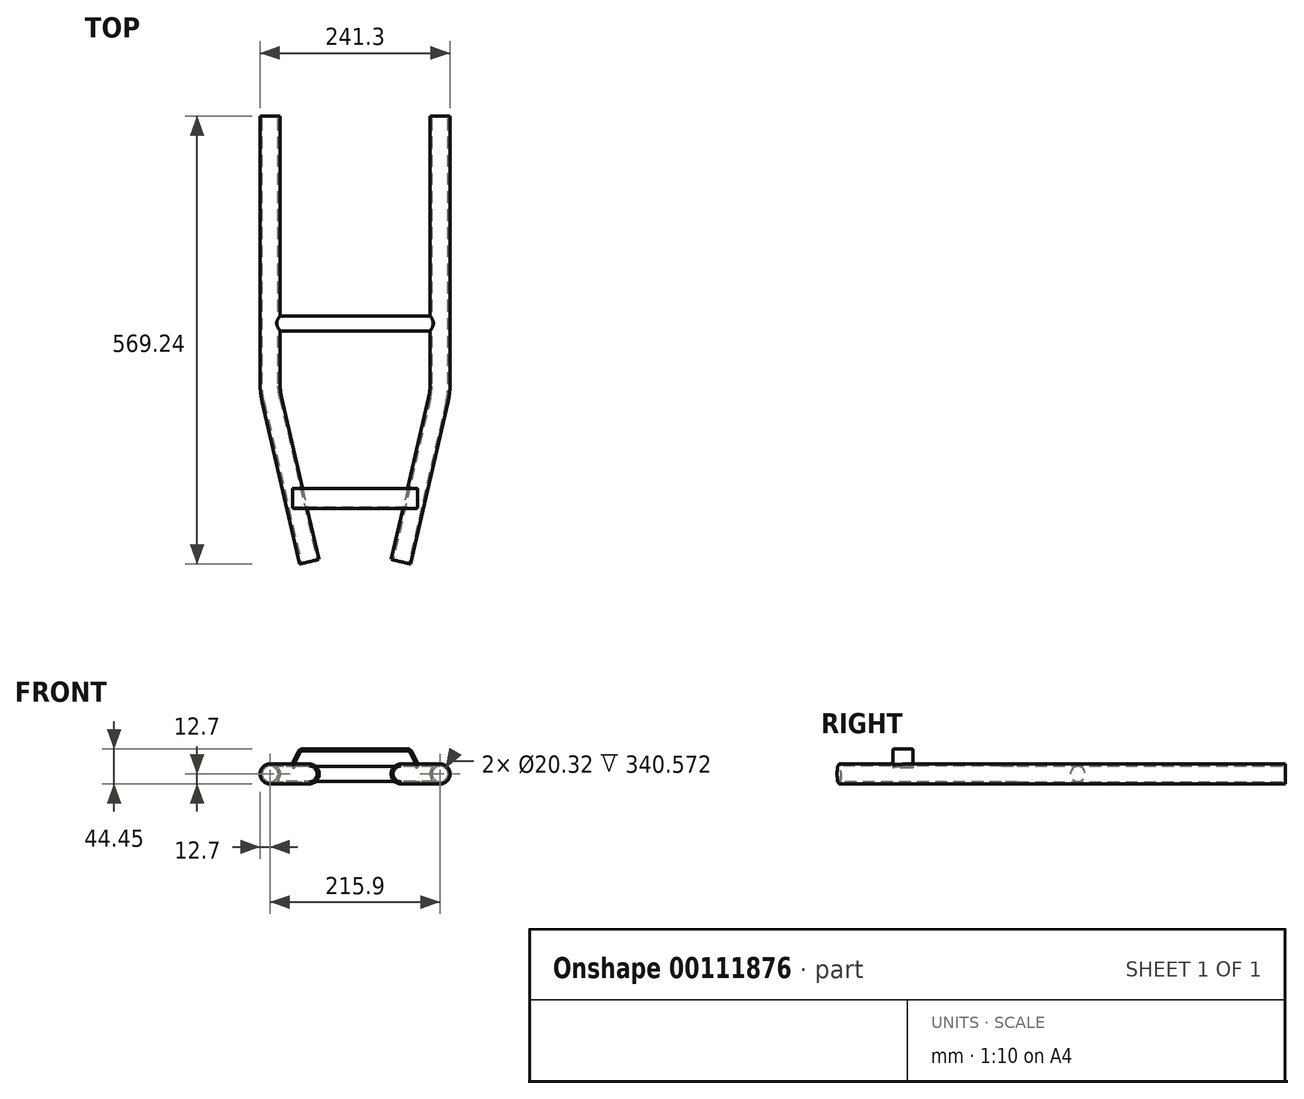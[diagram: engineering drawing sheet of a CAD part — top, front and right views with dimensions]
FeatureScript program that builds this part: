
annotation { "Feature Type Name" : "Feature", "Feature Type Description" : "" }
export const myFeature = defineFeature(function(context is Context, id is Id, definition is map)
    precondition{}
    {
        {
            var Q0;
            Q0=qCreatedBy(makeId("Top.planeOp"),FACE);
            var sketch = newSketch(context, id + "F0", { "sketchPlane" : qUnion([Q0])});
            skLineSegment(sketch, "E0", {"start": v(-95.25, 0) * mm, "end": v(-95.25, 273.05) * mm});
            skLineSegment(sketch, "E1", {"start": v(-95.25, 0) * mm, "end": v(-95.25, -67.52) * mm});
            skLineSegment(sketch, "E2", {"start": v(-93.3, -84.66) * mm, "end": v(-66.67, -200.03) * mm});
            skLineSegment(sketch, "E3", {"start": v(-66.67, -200.03) * mm, "end": v(-45.8, -290.48) * mm});
            skPoint(sketch, "E4.visualSharp", {"position": v(-95.25, -76.2) * mm});
            skArc(sketch, "E4.filletArc", {"start": v(-95.25, -67.52) * mm, "mid": v(-94.76, -76.14) * mm, "end": v(-93.3, -84.66) * mm});
            skSolve(sketch);
        }
        {
            var Q0;
            Q0=qCreatedBy(makeId("Front.planeOp"),FACE);
            var sketch = newSketch(context, id + "F1", { "sketchPlane" : qUnion([Q0])});
            skLineSegment(sketch, "E5", {"start": v(-95.25, 0) * mm, "end": v(-107.95, 0) * mm, "construction": true});
            skCircle(sketch, "E6", {"center": v(-107.95, 0) * mm, "radius": 12.7 * mm});
            skCircle(sketch, "E7", {"center": v(-107.95, 0) * mm, "radius": 10.16 * mm});
            skSolve(sketch);
        }
        {
            var Q0;
            Q0=makeQuery(id+"F1.imprint","IMPRINT",FACE,{"disambiguationData":[TD([[makeQuery(id+"F1.imprint","IMPRINT",EDGE,{"derivedFrom":sQuery(id+"F1.wireOp",EDGE,"E6")}),1.0]])]});
            var Q1;
            Q1=sQuery(id+"F0.wireOp",EDGE,"E0");
            sweep(context, id + "F2", {"profiles" : qUnion([Q0]), "path" : qUnion([Q1])});
        }
        {
            var Q0;
            Q0 = qSketchRegion(id + "F1", true);
            var Q1;
            Q1=sQuery(id+"F0.wireOp",EDGE,"E1");
            var Q2;
            Q2=sQuery(id+"F0.wireOp",EDGE,"E2");
            var Q3;
            Q3=sQuery(id+"F0.wireOp",EDGE,"E3");
            var Q4;
            Q4=sQuery(id+"F0.wireOp",EDGE,"E4.filletArc");
            sweep(context, id + "F3", {"operationType" : NewBodyOperationType.ADD, "profiles" : qUnion([Q0]), "path" : qUnion([Q1, Q2, Q3, Q4])});
        }
        {
            var Q0;
            Q0=sQuery(id+"F0.wireOp",VERTEX,"E3.start");
            var Q1;
            Q1=qCreatedBy(makeId("Front.planeOp"),FACE);
            cPlane(context, id + "F4", {"entities" : qUnion([Q0, Q1]), "cplaneType" : CPlaneType.PLANE_POINT, "offset" : 25.4 * mm, "width" : 152.4 * mm, "height" : 152.4 * mm});
        }
        {
            var Q0;
            Q0=qCreatedBy(id+"F4.planeOp",FACE);
            var sketch = newSketch(context, id + "F5", { "sketchPlane" : qUnion([Q0])});
            skLineSegment(sketch, "E8", {"start": v(-66.67, 0) * mm, "end": v(-79.37, 0) * mm, "construction": true});
            skLineSegment(sketch, "E9", {"start": v(-79.37, 0) * mm, "end": v(-79.37, 12.7) * mm, "construction": true});
            skLineSegment(sketch, "E10", {"start": v(0, 0) * mm, "end": v(0, 64.72) * mm, "construction": true});
            skLineSegment(sketch, "E11", {"start": v(-78.7, 15.54) * mm, "end": v(-72.35, 28.24) * mm});
            skLineSegment(sketch, "E12", {"start": v(-66.67, 31.75) * mm, "end": v(0, 31.75) * mm});
            skPoint(sketch, "E13.visualSharp", {"position": v(-70.6, 31.75) * mm});
            skArc(sketch, "E13.filletArc", {"start": v(-66.67, 31.75) * mm, "mid": v(-70.01, 30.8) * mm, "end": v(-72.35, 28.24) * mm});
            skArc(sketch, "E14.filletArc", {"start": v(-78.7, 15.54) * mm, "mid": v(-79.2, 14.16) * mm, "end": v(-79.37, 12.7) * mm});
            skLineSegment(sketch, "E15", {"start": v(-79.37, 12.7) * mm, "end": v(-79.37, 7.46) * mm});
            skSolve(sketch);
        }
        {
            var Q0;
            Q0=qCreatedBy(makeId("Right.planeOp"),FACE);
            var sketch = newSketch(context, id + "F6", { "sketchPlane" : qUnion([Q0])});
            skLineSegment(sketch, "E16", {"start": v(-200.03, 29.2) * mm, "end": v(-200.03, 30.48) * mm});
            skLineSegment(sketch, "E17", {"start": v(-201.3, 31.75) * mm, "end": v(-224.16, 31.75) * mm});
            skLineSegment(sketch, "E18", {"start": v(-225.43, 30.48) * mm, "end": v(-225.43, 29.2) * mm});
            skPoint(sketch, "E19.visualSharp", {"position": v(-200.03, 31.75) * mm});
            skArc(sketch, "E19.filletArc", {"start": v(-200.03, 30.48) * mm, "mid": v(-200.4, 31.38) * mm, "end": v(-201.3, 31.75) * mm});
            skPoint(sketch, "E20.visualSharp", {"position": v(-225.43, 31.75) * mm});
            skArc(sketch, "E20.filletArc", {"start": v(-224.16, 31.75) * mm, "mid": v(-225.05, 31.38) * mm, "end": v(-225.43, 30.48) * mm});
            skLineSegment(sketch, "E21.0", {"start": v(-224.66, 30.48) * mm, "end": v(-224.66, 29.2) * mm});
            skLineSegment(sketch, "E21.1", {"start": v(-200.79, 29.2) * mm, "end": v(-200.79, 30.48) * mm});
            skArc(sketch, "E21.2", {"start": v(-200.79, 30.48) * mm, "mid": v(-200.94, 30.84) * mm, "end": v(-201.3, 30.99) * mm});
            skLineSegment(sketch, "E21.3", {"start": v(-201.3, 30.99) * mm, "end": v(-224.16, 30.99) * mm});
            skArc(sketch, "E21.4", {"start": v(-224.16, 30.99) * mm, "mid": v(-224.51, 30.84) * mm, "end": v(-224.66, 30.48) * mm});
            skLineSegment(sketch, "E22", {"start": v(-200.03, 29.2) * mm, "end": v(-200.79, 29.2) * mm});
            skLineSegment(sketch, "E23", {"start": v(-224.66, 29.2) * mm, "end": v(-225.43, 29.2) * mm});
            skSolve(sketch);
        }
        {
            var Q0;
            Q0=makeQuery(id+"F6.imprint","IMPRINT",FACE,{"disambiguationData":[TD([[makeQuery(id+"F6.imprint","IMPRINT",EDGE,{"derivedFrom":sQuery(id+"F6.wireOp",EDGE,"E16")}),1.0]])]});
            var Q1;
            Q1=sQuery(id+"F5.wireOp",EDGE,"E12");
            var Q2;
            Q2=sQuery(id+"F5.wireOp",EDGE,"E13.filletArc");
            var Q3;
            Q3=sQuery(id+"F5.wireOp",EDGE,"E11");
            var Q4;
            Q4=sQuery(id+"F5.wireOp",EDGE,"E14.filletArc");
            var Q5;
            Q5=sQuery(id+"F5.wireOp",EDGE,"E15");
            sweep(context, id + "F7", {"operationType" : NewBodyOperationType.ADD, "profiles" : qUnion([Q0]), "path" : qUnion([Q1, Q2, Q3, Q4, Q5])});
        }
        {
            var Q0;
            Q0=makeQuery(id+"F2.opSweep","SWEPT_BODY",BODY,{"disambiguationData":[OSD([sQuery(id+"F0.wireOp",EDGE,"E0"),sQuery(id+"F1.wireOp",EDGE,"E6")])]});
            var Q1;
            Q1=qCreatedBy(makeId("Right.planeOp"),FACE);
            mirror(context, id + "F8", {"entities" : qUnion([Q0]), "mirrorPlane" : qUnion([Q1])});
        }
        {
            var Q0;
            Q0=qCreatedBy(makeId("Right.planeOp"),FACE);
            var sketch = newSketch(context, id + "F9", { "sketchPlane" : qUnion([Q0])});
            skLineSegment(sketch, "E24", {"start": v(0, 0) * mm, "end": v(9.53, 0) * mm, "construction": true});
            skCircle(sketch, "E25", {"center": v(9.53, 0) * mm, "radius": 9.53 * mm});
            skSolve(sketch);
        }
        {
            var Q0;
            Q0=makeQuery(id+"F9.imprint","IMPRINT",FACE,{"disambiguationData":[TD([[makeQuery(id+"F9.imprint","IMPRINT",EDGE,{"derivedFrom":sQuery(id+"F9.wireOp",EDGE,"E25")}),1.0]])]});
            extrude(context, id + "F10", {"entities" : qUnion([Q0]), "operationType" : NewBodyOperationType.ADD, "endBound" : BoundingType.UP_TO_NEXT, "depth" : 25.4 * mm, "hasSecondDirection" : true, "secondDirectionBound" : SecondDirectionBoundingType.UP_TO_NEXT, "secondDirectionOppositeDirection" : true, "secondDirectionDepth" : 25.4 * mm});
        }
    });
